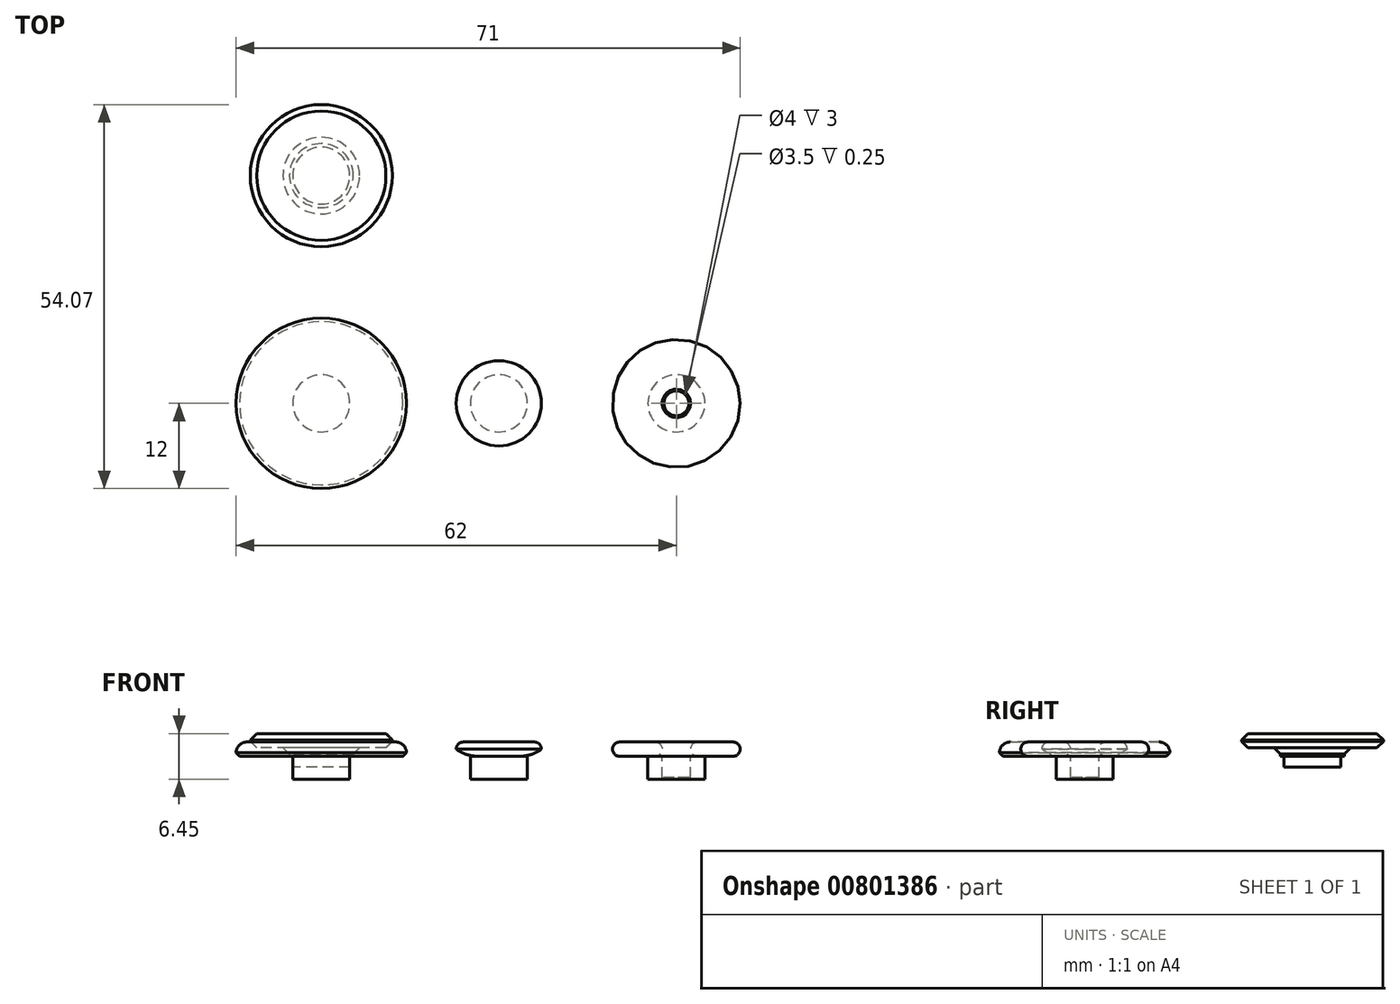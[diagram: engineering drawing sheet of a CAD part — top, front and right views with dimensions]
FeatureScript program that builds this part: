
annotation { "Feature Type Name" : "Feature", "Feature Type Description" : "" }
export const myFeature = defineFeature(function(context is Context, id is Id, definition is map)
    precondition{}
    {
        {
            var Q0;
            Q0=qCreatedBy(makeId("Top.planeOp"),FACE);
            var sketch = newSketch(context, id + "F0", { "sketchPlane" : qUnion([Q0])});
            skCircle(sketch, "E0", {"center": v(0, 0) * mm, "radius": 4.02 * mm});
            skCircle(sketch, "E1.1.0.0", {"center": v(25, 0) * mm, "radius": 4.02 * mm});
            skCircle(sketch, "E1.2.0.0", {"center": v(50, 0) * mm, "radius": 4.02 * mm});
            skLineSegment(sketch, "E1.direction1", {"start": v(0, 0) * mm, "end": v(25, 0) * mm, "construction": true});
            skSolve(sketch);
        }
        {
            var Q0;
            Q0=makeQuery(id+"F0.imprint","IMPRINT",FACE,{"disambiguationData":[TD([[makeQuery(id+"F0.imprint","IMPRINT",EDGE,{"derivedFrom":sQuery(id+"F0.wireOp",EDGE,"E0")}),1.0]])]});
            var Q1;
            Q1=makeQuery(id+"F0.imprint","IMPRINT",FACE,{"disambiguationData":[TD([[makeQuery(id+"F0.imprint","IMPRINT",EDGE,{"derivedFrom":sQuery(id+"F0.wireOp",EDGE,"E1.1.0.0")}),1.0]])]});
            var Q2;
            Q2=makeQuery(id+"F0.imprint","IMPRINT",FACE,{"disambiguationData":[TD([[makeQuery(id+"F0.imprint","IMPRINT",EDGE,{"derivedFrom":sQuery(id+"F0.wireOp",EDGE,"E1.2.0.0")}),1.0]])]});
            extrude(context, id + "F1", {"entities" : qUnion([Q0, Q1, Q2]), "oppositeDirection" : true, "depth" : 3.25 * mm, "offsetDistance" : 25 * mm});
        }
        {
            var Q0;
            Q0=qCreatedBy(makeId("Top.planeOp"),FACE);
            var sketch = newSketch(context, id + "F2", { "sketchPlane" : qUnion([Q0])});
            skCircle(sketch, "E2", {"center": v(0, 0) * mm, "radius": 12 * mm});
            skCircle(sketch, "E3", {"center": v(25, 0) * mm, "radius": 6 * mm});
            skCircle(sketch, "E4", {"center": v(50, 0) * mm, "radius": 9 * mm});
            skSolve(sketch);
        }
        {
            var Q0;
            Q0=makeQuery(id+"F2.imprint","IMPRINT",FACE,{"disambiguationData":[TD([[makeQuery(id+"F2.imprint","IMPRINT",EDGE,{"derivedFrom":sQuery(id+"F2.wireOp",EDGE,"E2")}),1.0]])]});
            var Q1;
            Q1=makeQuery(id+"F2.imprint","IMPRINT",FACE,{"disambiguationData":[TD([[makeQuery(id+"F2.imprint","IMPRINT",EDGE,{"derivedFrom":sQuery(id+"F2.wireOp",EDGE,"E3")}),1.0]])]});
            var Q2;
            Q2=makeQuery(id+"F2.imprint","IMPRINT",FACE,{"disambiguationData":[TD([[makeQuery(id+"F2.imprint","IMPRINT",EDGE,{"derivedFrom":sQuery(id+"F2.wireOp",EDGE,"E4")}),1.0]])]});
            extrude(context, id + "F3", {"entities" : qUnion([Q0, Q1, Q2]), "depth" : 2 * mm, "offsetDistance" : 25 * mm});
        }
        {
            var Q0;
            Q0=makeQuery(id+"F3.opExtrude","CAP_EDGE",EDGE,{"disambiguationData":[OSD([sQuery(id+"F2.wireOp",EDGE,"E2")])],"isStart":false});
            fillet(context, id + "F4", {"entities" : qUnion([Q0]), "radius" : 1.5 * mm, "tangentPropagation" : true, "allowEdgeOverflow" : false});
        }
        {
            var Q0;
            Q0=makeQuery(id+"F3.opExtrude","CAP_FACE",FACE,{"disambiguationData":[OSD([sQuery(id+"F2.wireOp",EDGE,"E2")])],"isStart":true});
            chamfer(context, id + "F5", {"entities" : qUnion([Q0]), "width" : .5 * mm, "tangentPropagation" : true});
        }
        {
            var Q0;
            Q0=makeQuery(id+"F3.opExtrude","CAP_FACE",FACE,{"disambiguationData":[OSD([sQuery(id+"F2.wireOp",EDGE,"E3")])],"isStart":false});
            fillet(context, id + "F6", {"entities" : qUnion([Q0]), "radius" : 1 * mm, "tangentPropagation" : true, "allowEdgeOverflow" : false});
        }
        {
            var Q0;
            Q0=makeQuery(id+"F3.opExtrude","CAP_FACE",FACE,{"disambiguationData":[OSD([sQuery(id+"F2.wireOp",EDGE,"E3")])],"isStart":true});
            fillet(context, id + "F7", {"entities" : qUnion([Q0]), "radius" : 5 * mm, "tangentPropagation" : true, "allowEdgeOverflow" : false});
        }
        {
            var Q0;
            Q0=makeQuery(id+"F3.opExtrude","CAP_FACE",FACE,{"disambiguationData":[OSD([sQuery(id+"F2.wireOp",EDGE,"E4")])],"isStart":false});
            var sketch = newSketch(context, id + "F8", { "sketchPlane" : qUnion([Q0])});
            skCircle(sketch, "E5", {"center": v(50, 0) * mm, "radius": 2 * mm});
            skSolve(sketch);
        }
        {
            var Q0;
            Q0=makeQuery(id+"F8.imprint","IMPRINT",FACE,{"disambiguationData":[TD([[makeQuery(id+"F8.imprint","IMPRINT",EDGE,{"derivedFrom":sQuery(id+"F8.wireOp",EDGE,"E5")}),1.0]])]});
            extrude(context, id + "F9", {"entities" : qUnion([Q0]), "operationType" : NewBodyOperationType.REMOVE, "oppositeDirection" : true, "depth" : 5 * mm, "offsetDistance" : 25 * mm});
        }
        {
            var Q0;
            Q0=makeQuery(id+"F1.opExtrude","CAP_FACE",FACE,{"disambiguationData":[OSD([sQuery(id+"F0.wireOp",EDGE,"E1.2.0.0")])],"isStart":true});
            var sketch = newSketch(context, id + "F10", { "sketchPlane" : qUnion([Q0])});
            skCircle(sketch, "E6", {"center": v(50, 0) * mm, "radius": 1.75 * mm});
            skSolve(sketch);
        }
        {
            var Q0;
            Q0=makeQuery(id+"F10.imprint","IMPRINT",FACE,{"disambiguationData":[TD([[makeQuery(id+"F10.imprint","IMPRINT",EDGE,{"derivedFrom":sQuery(id+"F10.wireOp",EDGE,"E6")}),1.0]])]});
            extrude(context, id + "F11", {"entities" : qUnion([Q0]), "operationType" : NewBodyOperationType.REMOVE, "oppositeDirection" : true, "depth" : 25 * mm, "offsetDistance" : 25 * mm});
        }
        {
            var Q0;
            Q0=makeQuery(id+"F3.opExtrude","CAP_FACE",FACE,{"disambiguationData":[OSD([sQuery(id+"F2.wireOp",EDGE,"E4")])],"isStart":false});
            var Q1;
            Q1=makeQuery(id+"F3.opExtrude","CAP_FACE",FACE,{"disambiguationData":[OSD([sQuery(id+"F2.wireOp",EDGE,"E4")])],"isStart":true});
            fillet(context, id + "F12", {"entities" : qUnion([Q0, Q1]), "radius" : 1 * mm, "tangentPropagation" : true, "allowEdgeOverflow" : false});
        }
        {
            var Q0;
            Q0=qCreatedBy(makeId("Top.planeOp"),FACE);
            var sketch = newSketch(context, id + "F13", { "sketchPlane" : qUnion([Q0])});
            skCircle(sketch, "E7", {"center": v(0, 32.07) * mm, "radius": 4 * mm});
            skSolve(sketch);
        }
        {
            var Q0;
            Q0=makeQuery(id+"F13.imprint","IMPRINT",FACE,{"disambiguationData":[TD([[makeQuery(id+"F13.imprint","IMPRINT",EDGE,{"derivedFrom":sQuery(id+"F13.wireOp",EDGE,"E7")}),1.0]])]});
            extrude(context, id + "F14", {"entities" : qUnion([Q0]), "oppositeDirection" : true, "depth" : 1.5 * mm, "offsetDistance" : 25 * mm});
        }
        {
            var Q0;
            Q0=makeQuery(id+"F14.opExtrude","CAP_FACE",FACE,{"disambiguationData":[OSD([sQuery(id+"F13.wireOp",EDGE,"E7")])],"isStart":true});
            var sketch = newSketch(context, id + "F15", { "sketchPlane" : qUnion([Q0])});
            skCircle(sketch, "E8", {"center": v(0, 32.07) * mm, "radius": 4.5 * mm});
            skSolve(sketch);
        }
        {
            var Q0;
            Q0=makeQuery(id+"F15.imprint","IMPRINT",FACE,{"disambiguationData":[TD([[makeQuery(id+"F15.imprint","IMPRINT",EDGE,{"derivedFrom":sQuery(id+"F15.wireOp",EDGE,"E8")}),1.0]])]});
            var Q1;
            Q1=makeQuery(id+"F15.imprint","IMPRINT",FACE,{"disambiguationData":[TD([[makeQuery(id+"F15.imprint","IMPRINT",EDGE,{"derivedFrom":makeQuery(id+"F14.opExtrude","CAP_EDGE",EDGE,{"disambiguationData":[OSD([sQuery(id+"F13.wireOp",EDGE,"E7")])],"isStart":true})}),1.0]])]});
            extrude(context, id + "F16", {"entities" : qUnion([Q0, Q1]), "operationType" : NewBodyOperationType.ADD, "depth" : 1.2 * mm, "offsetDistance" : 25 * mm});
        }
        {
            var Q0;
            Q0=makeQuery(id+"F16.opExtrude","CAP_FACE",FACE,{"disambiguationData":[OSD([sQuery(id+"F15.wireOp",EDGE,"E8")])],"isStart":false});
            var sketch = newSketch(context, id + "F17", { "sketchPlane" : qUnion([Q0])});
            skCircle(sketch, "E9", {"center": v(0, 32.07) * mm, "radius": 10 * mm});
            skSolve(sketch);
        }
        {
            var Q0;
            Q0=makeQuery(id+"F17.imprint","IMPRINT",FACE,{"disambiguationData":[TD([[makeQuery(id+"F17.imprint","IMPRINT",EDGE,{"derivedFrom":sQuery(id+"F17.wireOp",EDGE,"E9")}),1.0]])]});
            var Q1;
            Q1=makeQuery(id+"F17.imprint","IMPRINT",FACE,{"disambiguationData":[TD([[makeQuery(id+"F17.imprint","IMPRINT",EDGE,{"derivedFrom":makeQuery(id+"F16.opExtrude","CAP_EDGE",EDGE,{"disambiguationData":[OSD([sQuery(id+"F15.wireOp",EDGE,"E8")])],"isStart":false})}),1.0]])]});
            extrude(context, id + "F18", {"entities" : qUnion([Q0, Q1]), "operationType" : NewBodyOperationType.ADD, "depth" : 2 * mm, "offsetDistance" : 25 * mm});
        }
        {
            var Q0;
            Q0=makeQuery(id+"F18.opExtrude","CAP_FACE",FACE,{"disambiguationData":[OSD([sQuery(id+"F17.wireOp",EDGE,"E9")])],"isStart":true});
            chamfer(context, id + "F19", {"entities" : qUnion([Q0]), "width" : .9 * mm, "tangentPropagation" : true});
        }
        {
            var Q0;
            Q0=makeQuery(id+"F18.opExtrude","CAP_FACE",FACE,{"disambiguationData":[OSD([sQuery(id+"F17.wireOp",EDGE,"E9")])],"isStart":false});
            chamfer(context, id + "F20", {"entities" : qUnion([Q0]), "width" : .9 * mm, "tangentPropagation" : true});
        }
    });
